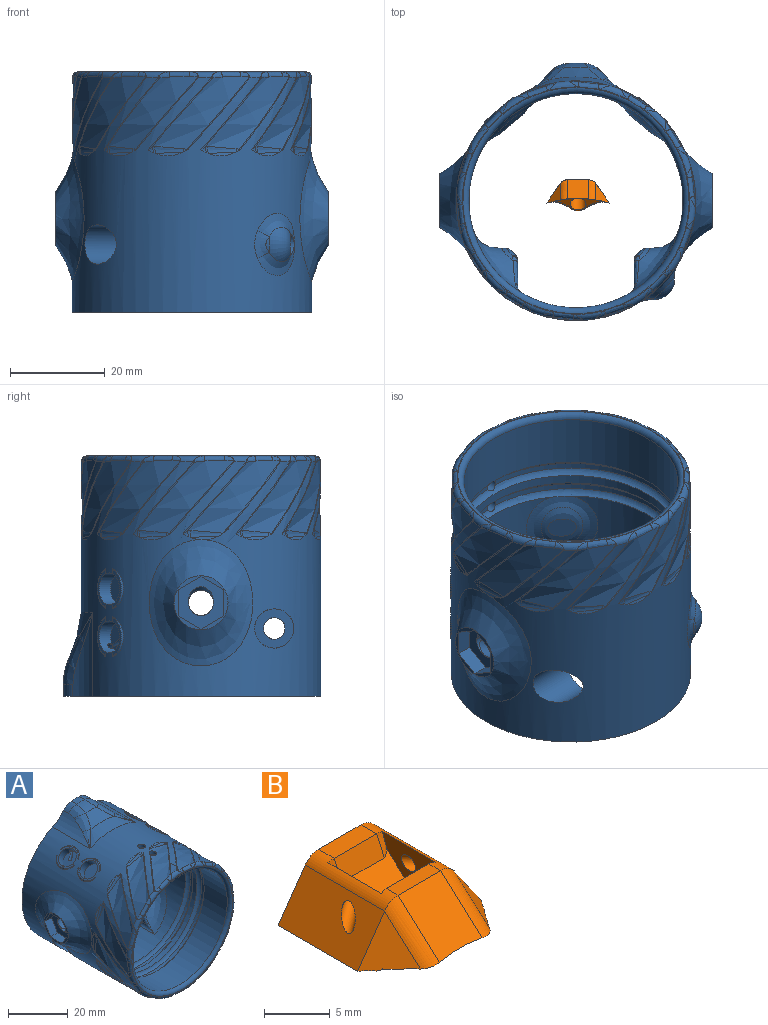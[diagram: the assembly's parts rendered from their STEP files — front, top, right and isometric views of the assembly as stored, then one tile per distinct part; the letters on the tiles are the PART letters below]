
ASSEMBLY  parts=2 mates=1
PART A: 355 faces, bbox 63.7x57.1x64.7 mm
  f0: torus R=24.04mm, axis (0,1,0), area 8.6mm2, adj f1,f340,f341,f342
  f1: bspline ~2.94x2.07mm, area 2.1mm2, adj f0,f2,f338,f339
  f2: bspline ~17.02x11.91mm, area 4.5mm2, adj f1,f3,f338,f342
  f3: bspline ~0.75x0.46mm, area 0mm2, adj f2,f4,f342
  f4: bspline ~0.8x0.72mm, area 0.3mm2, adj f3,f5,f338,f342
  f5: bspline ~7.78x2.13mm, area 6.8mm2, adj f4,f6,f337,f338
  f6: bspline ~1.52x0.62mm, area 0.7mm2, adj f5,f7,f338,f342
  f7: bspline ~1.74x1.53mm, area 0.7mm2, adj f6,f8,f342
  f8: bspline ~17.1x14.23mm, area 4.4mm2, adj f7,f9,f338,f342
  f9: bspline ~2.71x2.04mm, area 2.8mm2, adj f8,f10,f338,f339
  f10: torus R=24.04mm, axis (0,1,0), area 8.6mm2, adj f9,f11,f340,f342
  f11: bspline ~3.16x1.68mm, area 2.1mm2, adj f10,f12,f335,f336
  f12: bspline ~15.19x13mm, area 3.8mm2, adj f11,f13,f335,f342
  f13: cylinder r=1.27mm len=2.54mm, axis (0,0,-1), area 11.9mm2, adj f12,f14,f331,f334,f335,f342
  f14: torus R=22.14mm, axis (0,1,0), area 244.3mm2, adj f13,f15,f334
  f15: cylinder r=22.64mm len=45.29mm, axis (0,1,0), area 274.1mm2, adj f14,f16
  f16: torus R=22.14mm, axis (0,1,0), area 244.3mm2, adj f15,f17,f330
  f17: cylinder r=23.81mm len=47.63mm, axis (0,1,0), area 174.6mm2, adj f16,f18,f330
  f18: torus R=22.14mm, axis (0,1,0), area 243.9mm2, adj f17,f19,f25,f327,f330
  f19: bspline ~14.78x11.6mm, area 99.1mm2, adj f18,f20,f23,f25
  f20: bspline ~14.78x11.6mm, area 99.2mm2, adj f19,f21,f25
  f21: bspline ~9.62x6.81mm, area 48.2mm2, adj f20,f22
  f22: plane 4.62x4.43mm, normal (-0.64,0,-0.77), area 21.5mm2, adj f21
  f23: bspline ~9.62x6.81mm, area 48.2mm2, adj f19,f24
  f24: plane 4.62x4.43mm, normal (-0.64,0,-0.77), area 21.5mm2, adj f23
  f25: cylinder r=22.64mm len=45.29mm, axis (0,1,0), area 2511.8mm2, adj f18,f19,f20,f26,f52,f53,f54,f55
  f26: cylinder r=4.15mm len=8.31mm, axis (-1,0,0), area 147.8mm2, adj f25,f27,f40,f41,f42,f43,f44,f52
  f27: cylinder r=1.27mm len=1.9mm, axis (0,-1,0), area 0.9mm2, adj f26,f28,f40,f43
  f28: bspline ~1.21x1.2mm, area 0.4mm2, adj f27,f29,f39
  f29: bspline ~7.99x2.24mm, area 9.1mm2, adj f28,f30,f37,f38,f39,f43
  f30: cylinder r=5.42mm len=9.09mm, axis (-1,0,0), area 10.2mm2, adj f29,f31,f34,f53
  f31: torus R=4.41mm, axis (1,0,0), area 1.3mm2, adj f30,f32,f39,f40
  f32: bspline ~6.55x4.88mm, area 8.1mm2, adj f31,f33,f40,f53
  f33: bspline ~5.6x2.57mm, area 2.4mm2, adj f32,f52,f53
  f34: torus R=4.41mm, axis (1,0,0), area 1.3mm2, adj f30,f35,f37,f41
  f35: bspline ~6.55x4.88mm, area 8.1mm2, adj f34,f36,f41,f53
  f36: bspline ~4.89x2.08mm, area 2.4mm2, adj f35,f53,f54
  f37: bspline ~1.33x1.3mm, area 0.3mm2, adj f29,f34,f38,f41
  f38: bspline ~1.21x1.2mm, area 0.4mm2, adj f29,f37,f42
  f39: bspline ~1.05x0.91mm, area 0.3mm2, adj f28,f29,f31,f40
  f40: plane 5.75x4.22mm, normal (-1,0,0), area 6.7mm2, adj f26,f27,f31,f32,f39,f52
  f41: plane 5.74x4.21mm, normal (-1,0,0), area 6.7mm2, adj f26,f34,f35,f37,f42,f54
  f42: cylinder r=1.27mm len=1.9mm, axis (0,-1,0), area 0.9mm2, adj f26,f38,f41,f43
  f43: plane 6x1.48mm, normal (-0.71,0,0.71), area 5.5mm2, adj f26,f27,f29,f42
  f44: plane 8.31x8.31mm, normal (-1,0,0), area 37.8mm2, adj f26,f45
  f45: cylinder r=2.29mm len=4.57mm, axis (-1,0,0), area 44.4mm2, adj f44,f46,f49,f50,f51
  f46: torus R=0.85mm, axis (1,0,0), area 38mm2, adj f45,f47,f49,f51
  f47: cylinder r=5.42mm len=3.31mm, axis (-1,0,0), area 0mm2, adj f46,f48
  f48: bspline ~7.72x3.76mm, area 13.3mm2, adj f47,f49,f51,f342
  f49: bspline ~8.2x8.04mm, area 33.9mm2, adj f45,f46,f48,f50,f342
  f50: cylinder r=4.57mm len=1.7mm, axis (0,1,0), area 0.2mm2, adj f45,f49,f51,f342
  f51: bspline ~8.09x7.87mm, area 33.9mm2, adj f45,f46,f48,f50,f342
  f52: cylinder r=1.52mm len=10.75mm, axis (0,1,0), area 11.5mm2, adj f25,f26,f33,f40
  f53: bspline ~24.01x16.87mm, area 259.2mm2, adj f25,f30,f32,f33,f35,f36,f54
  f54: cylinder r=1.52mm len=10.75mm, axis (0,1,0), area 10.8mm2, adj f25,f26,f36,f41,f53
  f55: cylinder r=1.52mm len=10.75mm, axis (0,1,0), area 10.8mm2, adj f25,f56,f72,f73,f75
  f56: bspline ~4.89x2.08mm, area 2.4mm2, adj f55,f57,f75
  f57: bspline ~6.55x4.88mm, area 8.1mm2, adj f56,f58,f72,f75
  f58: torus R=4.41mm, axis (1,0,0), area 1.3mm2, adj f57,f59,f71,f72
  f59: bspline ~1.28x1.27mm, area 0.3mm2, adj f58,f60,f70,f72
  f60: bspline ~1.21x1.2mm, area 0.4mm2, adj f59,f61,f70
  f61: cylinder r=1.27mm len=1.9mm, axis (0,-1,0), area 0.9mm2, adj f60,f62,f72,f73
  f62: plane 6x1.48mm, normal (0.71,0,0.71), area 5.5mm2, adj f61,f63,f70,f73
  f63: cylinder r=1.27mm len=1.9mm, axis (0,-1,0), area 0.9mm2, adj f62,f64,f69,f73
  f64: plane 5.74x4.21mm, normal (1,0,0), area 6.7mm2, adj f63,f65,f67,f68,f73,f74
  f65: bspline ~6.55x4.88mm, area 8.1mm2, adj f64,f66,f67,f75
  f66: bspline ~5.6x2.57mm, area 2.4mm2, adj f65,f74,f75
  f67: torus R=4.41mm, axis (1,0,0), area 1.3mm2, adj f64,f65,f68,f71
  f68: bspline ~1.33x1.3mm, area 0.3mm2, adj f64,f67,f69,f70
  f69: bspline ~1.21x1.2mm, area 0.4mm2, adj f63,f68,f70
  f70: bspline ~7.99x2.24mm, area 9.1mm2, adj f59,f60,f62,f68,f69,f71
  f71: cylinder r=5.42mm len=9.09mm, axis (-1,0,0), area 10.2mm2, adj f58,f67,f70,f75
  f72: plane 5.75x4.22mm, normal (1,0,0), area 6.7mm2, adj f55,f57,f58,f59,f61,f73
  f73: cylinder r=4.15mm len=11.06mm, axis (-1,0,0), area 190.1mm2, adj f25,f55,f61,f62,f63,f64,f72,f74
  f74: cylinder r=1.52mm len=10.75mm, axis (0,1,0), area 11.5mm2, adj f25,f64,f66,f73
  f75: bspline ~24.01x16.87mm, area 259.2mm2, adj f25,f55,f56,f57,f65,f66,f71
  f76: cylinder r=5.71mm len=11.43mm, axis (1,0,0), area 14mm2, adj f25,f77
  f77: plane 17.49x17.49mm, normal (1,0,0), area 72.9mm2, adj f76,f78,f266
  f78: cylinder r=2.67mm len=5.33mm, axis (1,0,0), area 21.1mm2, adj f77,f79,f80,f266
  f79: cylinder r=2.63mm len=5.26mm, axis (-0.87,-0.48,0), area 0mm2, adj f78,f80
  f80: plane 13.99x12.5mm, normal (-1,0,0), area 55.1mm2, adj f78,f79,f81,f261,f262,f263,f264,f265
  f81: plane 4.85x3.32mm, normal (0,0.87,-0.5), area 18.4mm2, adj f80,f82,f260,f261,f265
  f82: plane 11.45x11.45mm, normal (-1,0,0), area 21.9mm2, adj f81,f83,f84,f260,f261,f262,f263,f264
  f83: cylinder r=2.63mm len=0.27mm, axis (-0.87,-0.48,0), area 0mm2, adj f82,f261
  f84: bspline ~26.69x21.89mm, area 456.4mm2, adj f82,f85,f342
  f85: bspline ~10.29x1.28mm, area 2.3mm2, adj f84,f86,f342
  f86: bspline ~9.05x1.63mm, area 7.1mm2, adj f85,f87,f258,f259,f342
  f87: bspline ~5.04x4.49mm, area 0.1mm2, adj f86,f88,f342
  f88: bspline ~16.54x13.1mm, area 4.2mm2, adj f87,f89,f258,f342
  f89: bspline ~3.13x1.68mm, area 2.1mm2, adj f88,f90,f229,f258
  f90: torus R=24.04mm, axis (0,1,0), area 8.6mm2, adj f89,f91,f340,f342
  f91: bspline ~2.91x1.57mm, area 2.8mm2, adj f90,f92,f227,f228
  f92: bspline ~7.63x5.22mm, area 6.7mm2, adj f91,f93,f227,f340
  f93: bspline ~2.61x2.46mm, area 2.1mm2, adj f92,f94,f220,f227
  f94: torus R=24.04mm, axis (0,1,0), area 8.6mm2, adj f93,f95,f340,f342
  f95: bspline ~2.87x1.53mm, area 2.8mm2, adj f94,f96,f218,f219
  f96: bspline ~8.34x1.89mm, area 6.7mm2, adj f95,f97,f218,f340
  f97: bspline ~2.88x1.68mm, area 2.1mm2, adj f96,f98,f211,f218
  f98: torus R=24.04mm, axis (0,1,0), area 8.6mm2, adj f97,f99,f340,f342
  f99: bspline ~2.65x1.92mm, area 2.8mm2, adj f98,f100,f209,f210
  f100: bspline ~8.12x3.87mm, area 6.7mm2, adj f99,f101,f209,f340
  f101: bspline ~3.16x1.68mm, area 2.1mm2, adj f100,f102,f202,f209
  f102: torus R=24.04mm, axis (0,1,0), area 8.6mm2, adj f101,f103,f340,f342
  f103: bspline ~2.71x2.04mm, area 2.8mm2, adj f102,f104,f200,f201
  f104: bspline ~6.69x6.53mm, area 6.7mm2, adj f103,f105,f200,f340
  f105: bspline ~2.94x2.07mm, area 2.1mm2, adj f104,f106,f193,f200
  f106: torus R=24.04mm, axis (0,1,0), area 8.6mm2, adj f105,f107,f340,f342
  f107: bspline ~2.96x1.53mm, area 2.8mm2, adj f106,f108,f191,f192
  f108: bspline ~6.73x3.14mm, area 6.7mm2, adj f107,f109,f191,f340
  f109: bspline ~2.74x2.14mm, area 2.1mm2, adj f108,f110,f184,f191
  f110: torus R=24.04mm, axis (0,1,0), area 8.6mm2, adj f109,f111,f340,f342
  f111: bspline ~2.76x1.53mm, area 2.8mm2, adj f110,f112,f182,f183
  f112: bspline ~8.32x2.12mm, area 6.7mm2, adj f111,f113,f182,f340
  f113: bspline ~3.03x1.68mm, area 2.1mm2, adj f112,f114,f175,f182
  f114: torus R=24.04mm, axis (0,1,0), area 8.6mm2, adj f113,f115,f340,f342
  f115: bspline ~2.4x2.38mm, area 2.8mm2, adj f114,f116,f173,f174
  f116: bspline ~7.51x5.42mm, area 6.7mm2, adj f115,f117,f173,f340
  f117: bspline ~3.13x1.68mm, area 2.1mm2, adj f116,f118,f152,f173
  f118: torus R=24.04mm, axis (0,1,0), area 8.6mm2, adj f117,f119,f340,f342
  f119: bspline ~2.91x1.57mm, area 2.8mm2, adj f118,f120,f150,f151
  f120: bspline ~7.63x5.22mm, area 6.7mm2, adj f119,f121,f150,f340
  f121: bspline ~2.61x2.46mm, area 2.1mm2, adj f120,f122,f143,f150
  f122: torus R=24.04mm, axis (0,1,0), area 8.6mm2, adj f121,f123,f340,f342
  f123: bspline ~2.87x1.53mm, area 2.8mm2, adj f122,f124,f141,f142
  f124: bspline ~8.34x1.89mm, area 6.7mm2, adj f123,f125,f141,f340
  f125: bspline ~2.88x1.68mm, area 2.1mm2, adj f124,f126,f134,f141
  f126: torus R=24.04mm, axis (0,1,0), area 8.6mm2, adj f125,f127,f133,f340
  f127: bspline ~2.65x1.92mm, area 2.8mm2, adj f126,f128,f335,f336
  f128: bspline ~17.1x15mm, area 4.4mm2, adj f127,f129,f133,f335,f342
  f129: bspline ~1.74x1.45mm, area 0.7mm2, adj f128,f130,f342
  f130: bspline ~1.52x0.58mm, area 0.7mm2, adj f129,f131,f335,f342
  f131: bspline ~8.28x1.82mm, area 7.1mm2, adj f130,f132,f335,f342
  f132: bspline ~10.13x2.46mm, area 0mm2, adj f131,f342
  f133: cylinder r=25.31mm len=4.47mm, axis (0,1,0), area 8mm2, adj f126,f128,f134,f342
  f134: bspline ~17.55x15.05mm, area 4.5mm2, adj f125,f133,f135,f141,f342
  f135: bspline ~0.71x0.46mm, area 0mm2, adj f134,f136,f342
  f136: bspline ~0.72x0.67mm, area 0.3mm2, adj f135,f137,f141,f342
  f137: bspline ~6.43x4.94mm, area 6.8mm2, adj f136,f138,f140,f141
  f138: bspline ~1.52x0.47mm, area 0.7mm2, adj f137,f139,f141,f342
  f139: bspline ~1.74x1.1mm, area 0.7mm2, adj f138,f142,f342
  f140: bspline ~8.36x6.55mm, area 0mm2, adj f137,f342
  f141: bspline ~24.34x17.78mm, area 120.3mm2, adj f123,f124,f125,f134,f136,f137,f138,f142
  f142: bspline ~17.1x12.79mm, area 4.4mm2, adj f123,f139,f141,f342
  f143: bspline ~17.55x12.01mm, area 4.5mm2, adj f121,f144,f150,f342
  f144: bspline ~0.66x0.48mm, area 0mm2, adj f143,f145,f342
  f145: bspline ~0.74x0.72mm, area 0.3mm2, adj f144,f146,f150,f342
  f146: bspline ~7.17x3.77mm, area 6.8mm2, adj f145,f147,f149,f150
  f147: bspline ~1.52x0.59mm, area 0.7mm2, adj f146,f148,f150,f342
  f148: bspline ~1.74x1.46mm, area 0.7mm2, adj f147,f151,f342
  f149: bspline ~9.34x4.93mm, area 0mm2, adj f146,f342
  f150: bspline ~19.46x17.78mm, area 120.3mm2, adj f119,f120,f121,f143,f145,f146,f147,f151
  f151: bspline ~17.1x12.76mm, area 4.4mm2, adj f119,f148,f150,f342
  f152: bspline ~16.54x13.1mm, area 4.2mm2, adj f117,f153,f173,f342
  f153: bspline ~5.07x4.52mm, area 0.1mm2, adj f152,f154,f342
  f154: bspline ~9.06x1.63mm, area 7.1mm2, adj f153,f155,f157,f173,f342
  f155: bspline ~1.52x0.62mm, area 0.7mm2, adj f154,f156,f173,f342
  f156: bspline ~1.74x1.53mm, area 0.7mm2, adj f155,f174,f342
  f157: bspline ~10.29x1.28mm, area 2.5mm2, adj f154,f158,f342
  f158: bspline ~26.69x21.9mm, area 456.4mm2, adj f157,f159,f342
  f159: plane 11.92x11.92mm, normal (1,0,0), area 22mm2, adj f158,f160,f166,f167,f168,f169,f170,f171
  f160: plane 5.57x3.3mm, normal (0,0,1), area 18.4mm2, adj f159,f161,f166,f171
  f161: plane 13.99x12.5mm, normal (1,0,0), area 55.1mm2, adj f160,f162,f165,f166,f167,f168,f170,f171
  f162: cylinder r=2.67mm len=5.33mm, axis (1,0,0), area 21.1mm2, adj f161,f163,f164,f165
  f163: plane 17.49x17.49mm, normal (-1,0,0), area 72.9mm2, adj f162,f164,f267
  f164: cylinder r=2.63mm len=5.26mm, axis (0.87,-0.48,0), area 0mm2, adj f162,f163
  f165: cylinder r=2.63mm len=5.26mm, axis (0.87,-0.48,0), area 0mm2, adj f161,f162
  f166: plane 4.83x3.3mm, normal (0,-0.87,0.5), area 18.4mm2, adj f159,f160,f161,f167
  f167: plane 4.83x3.3mm, normal (0,-0.87,-0.5), area 18.4mm2, adj f159,f161,f166,f168
  f168: plane 5.57x3.3mm, normal (0,0,-1), area 18.4mm2, adj f159,f161,f167,f170
  f169: cylinder r=2.63mm len=0.27mm, axis (0.87,-0.48,0), area 0mm2, adj f159,f170
  f170: plane 4.85x3.32mm, normal (0,0.87,-0.5), area 18.4mm2, adj f159,f161,f168,f169,f171
  f171: plane 4.85x3.32mm, normal (0,0.87,0.5), area 18.4mm2, adj f159,f160,f161,f170,f172
  f172: cylinder r=2.63mm len=0.27mm, axis (0.87,-0.48,0), area 0mm2, adj f159,f171
  f173: bspline ~25.19x17.78mm, area 120.2mm2, adj f115,f116,f117,f152,f154,f155,f174
  f174: bspline ~17.1x14.99mm, area 4.4mm2, adj f115,f156,f173,f342
  f175: bspline ~17.55x15.47mm, area 4.5mm2, adj f113,f176,f182,f342
  f176: bspline ~0.78x0.46mm, area 0mm2, adj f175,f177,f342
  f177: bspline ~0.74x0.72mm, area 0.3mm2, adj f176,f178,f182,f342
  f178: bspline ~7.32x3.42mm, area 6.8mm2, adj f177,f179,f181,f182
  f179: bspline ~1.52x0.53mm, area 0.7mm2, adj f178,f180,f182,f342
  f180: bspline ~1.74x1.29mm, area 0.7mm2, adj f179,f183,f342
  f181: bspline ~9.48x4.62mm, area 0mm2, adj f178,f342
  f182: bspline ~25.93x17.78mm, area 120.3mm2, adj f111,f112,f113,f175,f177,f178,f179,f183
  f183: bspline ~17.1x14.25mm, area 4.4mm2, adj f111,f180,f182,f342
  f184: bspline ~17.55x13.88mm, area 4.5mm2, adj f109,f185,f191,f342
  f185: bspline ~0.61x0.54mm, area 0mm2, adj f184,f186,f342
  f186: bspline ~0.72x0.64mm, area 0.3mm2, adj f185,f187,f191,f342
  f187: bspline ~6.21x5.21mm, area 6.8mm2, adj f186,f188,f190,f191
  f188: bspline ~1.52x0.54mm, area 0.7mm2, adj f187,f189,f191,f342
  f189: bspline ~1.74x1.31mm, area 0.7mm2, adj f188,f192,f342
  f190: bspline ~8.15x6.81mm, area 0mm2, adj f187,f342
  f191: bspline ~21.54x17.78mm, area 120.3mm2, adj f107,f108,f109,f184,f186,f187,f188,f192
  f192: bspline ~17.1x10.69mm, area 4.4mm2, adj f107,f189,f191,f342
  f193: bspline ~17.02x11.91mm, area 4.5mm2, adj f105,f194,f200,f342
  f194: bspline ~0.75x0.46mm, area 0mm2, adj f193,f195,f342
  f195: bspline ~0.8x0.72mm, area 0.3mm2, adj f194,f196,f200,f342
  f196: bspline ~7.78x2.13mm, area 6.8mm2, adj f195,f197,f199,f200
  f197: bspline ~1.52x0.62mm, area 0.7mm2, adj f196,f198,f200,f342
  f198: bspline ~1.74x1.53mm, area 0.7mm2, adj f197,f201,f342
  f199: bspline ~10.07x2.79mm, area 0mm2, adj f196,f342
  f200: bspline ~22.9x17.78mm, area 120.3mm2, adj f103,f104,f105,f193,f195,f196,f197,f201
  f201: bspline ~17.1x14.23mm, area 4.4mm2, adj f103,f198,f200,f342
  f202: bspline ~17.55x15.11mm, area 4.5mm2, adj f101,f203,f209,f342
  f203: bspline ~0.81x0.46mm, area 0mm2, adj f202,f204,f342
  f204: bspline ~0.79x0.72mm, area 0.3mm2, adj f203,f205,f209,f342
  f205: bspline ~7.86x1.74mm, area 6.8mm2, adj f204,f206,f208,f209
  f206: bspline ~1.52x0.58mm, area 0.7mm2, adj f205,f207,f209,f342
  f207: bspline ~1.74x1.45mm, area 0.7mm2, adj f206,f210,f342
  f208: bspline ~10.13x2.46mm, area 0mm2, adj f205,f342
  f209: bspline ~26.22x17.78mm, area 120.3mm2, adj f99,f100,f101,f202,f204,f205,f206,f210
  f210: bspline ~17.1x15mm, area 4.4mm2, adj f99,f207,f209,f342
  f211: bspline ~17.55x15.05mm, area 4.5mm2, adj f97,f212,f218,f342
  f212: bspline ~0.71x0.46mm, area 0mm2, adj f211,f213,f342
  f213: bspline ~0.72x0.67mm, area 0.3mm2, adj f212,f214,f218,f342
  f214: bspline ~6.43x4.94mm, area 6.8mm2, adj f213,f215,f217,f218
  f215: bspline ~1.52x0.47mm, area 0.7mm2, adj f214,f216,f218,f342
  f216: bspline ~1.74x1.1mm, area 0.7mm2, adj f215,f219,f342
  f217: bspline ~8.36x6.55mm, area 0mm2, adj f214,f342
  f218: bspline ~24.34x17.78mm, area 120.3mm2, adj f95,f96,f97,f211,f213,f214,f215,f219
  f219: bspline ~17.1x12.79mm, area 4.4mm2, adj f95,f216,f218,f342
  f220: bspline ~17.55x12.01mm, area 4.5mm2, adj f93,f221,f227,f342
  f221: bspline ~0.66x0.48mm, area 0mm2, adj f220,f222,f342
  f222: bspline ~0.74x0.72mm, area 0.3mm2, adj f221,f223,f227,f342
  f223: bspline ~7.17x3.77mm, area 6.8mm2, adj f222,f224,f226,f227
  f224: bspline ~1.52x0.59mm, area 0.7mm2, adj f223,f225,f227,f342
  f225: bspline ~1.74x1.46mm, area 0.7mm2, adj f224,f228,f342
  f226: bspline ~9.34x4.93mm, area 0mm2, adj f223,f342
  f227: bspline ~19.46x17.78mm, area 120.3mm2, adj f91,f92,f93,f220,f222,f223,f224,f228
  f228: bspline ~17.1x12.76mm, area 4.4mm2, adj f91,f225,f227,f342
  f229: bspline ~7.51x5.42mm, area 6.7mm2, adj f89,f230,f258,f340
  f230: bspline ~2.4x2.38mm, area 2.8mm2, adj f229,f231,f256,f258
  f231: torus R=24.04mm, axis (0,1,0), area 8.6mm2, adj f230,f232,f340,f342
  f232: bspline ~3.03x1.68mm, area 2.1mm2, adj f231,f233,f254,f255
  f233: bspline ~17.55x15.47mm, area 4.5mm2, adj f232,f234,f254,f342
  f234: bspline ~0.78x0.46mm, area 0mm2, adj f233,f235,f342
  f235: bspline ~0.74x0.72mm, area 0.3mm2, adj f234,f236,f254,f342
  f236: bspline ~7.32x3.42mm, area 6.8mm2, adj f235,f237,f253,f254
  f237: bspline ~1.52x0.53mm, area 0.7mm2, adj f236,f238,f254,f342
  f238: bspline ~1.74x1.29mm, area 0.7mm2, adj f237,f239,f342
  f239: bspline ~17.1x14.25mm, area 4.4mm2, adj f238,f240,f254,f342
  f240: bspline ~2.76x1.53mm, area 2.8mm2, adj f239,f241,f254,f255
  f241: torus R=24.04mm, axis (0,1,0), area 8.6mm2, adj f240,f242,f340,f342
  f242: bspline ~2.74x2.14mm, area 2.1mm2, adj f241,f243,f251,f252
  f243: bspline ~17.55x13.88mm, area 4.5mm2, adj f242,f244,f251,f342
  f244: bspline ~0.61x0.54mm, area 0mm2, adj f243,f245,f342
  f245: bspline ~0.72x0.64mm, area 0.3mm2, adj f244,f246,f251,f342
  f246: bspline ~6.21x5.21mm, area 6.8mm2, adj f245,f247,f250,f251
  f247: bspline ~1.52x0.54mm, area 0.7mm2, adj f246,f248,f251,f342
  f248: bspline ~1.74x1.31mm, area 0.7mm2, adj f247,f249,f342
  f249: bspline ~17.1x10.69mm, area 4.4mm2, adj f248,f251,f341,f342
  f250: bspline ~8.15x6.81mm, area 0mm2, adj f246,f342
  f251: bspline ~21.54x17.78mm, area 120.3mm2, adj f242,f243,f245,f246,f247,f249,f252,f341
  f252: bspline ~6.73x3.14mm, area 6.7mm2, adj f242,f251,f340,f341
  f253: bspline ~9.48x4.62mm, area 0mm2, adj f236,f342
  f254: bspline ~25.93x17.78mm, area 120.3mm2, adj f232,f233,f235,f236,f237,f239,f240,f255
  f255: bspline ~8.32x2.12mm, area 6.7mm2, adj f232,f240,f254,f340
  f256: bspline ~17.1x14.99mm, area 4.4mm2, adj f230,f257,f258,f342
  f257: bspline ~1.74x1.53mm, area 0.7mm2, adj f256,f259,f342
  f258: bspline ~25.19x17.78mm, area 120.2mm2, adj f86,f88,f89,f229,f230,f256,f259
  f259: bspline ~1.52x0.62mm, area 0.7mm2, adj f86,f257,f258,f342
  f260: cylinder r=2.63mm len=0.27mm, axis (-0.87,-0.48,0), area 0mm2, adj f81,f82
  f261: plane 4.85x3.32mm, normal (0,0.87,0.5), area 18.4mm2, adj f80,f81,f82,f83,f262
  f262: plane 5.57x3.3mm, normal (0,0,1), area 18.4mm2, adj f80,f82,f261,f263
  f263: plane 4.83x3.3mm, normal (0,-0.87,0.5), area 18.4mm2, adj f80,f82,f262,f264
  f264: plane 4.83x3.3mm, normal (0,-0.87,-0.5), area 18.4mm2, adj f80,f82,f263,f265
  f265: plane 5.57x3.3mm, normal (0,0,-1), area 18.4mm2, adj f80,f81,f82,f264
  f266: cylinder r=2.63mm len=5.26mm, axis (-0.87,-0.48,0), area 0mm2, adj f77,f78
  f267: cylinder r=5.71mm len=11.43mm, axis (1,0,0), area 14mm2, adj f25,f163
  f268: plane 5.1x5.03mm, normal (0.73,0.46,-0.51), area 16.4mm2, adj f25,f269,f285,f286,f287
  f269: plane 8.23x0.69mm, normal (0,-0.74,-0.67), area 0.7mm2, adj f268,f270,f273,f274,f281,f282,f284,f285
  f270: plane 4.06x3.42mm, normal (0.16,-0.99,0.04), area 1.4mm2, adj f269,f271,f272,f273,f293
  f271: plane 0.89x0.87mm, normal (0.23,-0.65,0.72), area 0.3mm2, adj f270,f272,f293,f294
  f272: plane 4.19x2.94mm, normal (0.73,-0.46,0.51), area 1mm2, adj f270,f271,f273,f274,f294
  f273: extruded ~0.4x0.32mm, area 0mm2, adj f269,f270,f272,f274
  f274: cylinder r=2.03mm len=8.49mm, axis (0,1,0), area 14.4mm2, adj f269,f272,f273,f275,f278,f279,f280,f281
  f275: plane 5.9x0.63mm, normal (0,0.67,-0.74), area 3.7mm2, adj f274,f276,f277,f278,f281,f282
  f276: cylinder r=1.27mm len=5.84mm, axis (-1,0,0), area 11.7mm2, adj f275,f277,f278,f279
  f277: plane 2.76x0.85mm, normal (1,0,0), area 1.5mm2, adj f275,f276,f279,f282
  f278: plane 2.76x0.85mm, normal (-1,0,0), area 1.5mm2, adj f274,f275,f276,f279
  f279: plane 5.89x0.48mm, normal (0,-0.74,-0.67), area 2.6mm2, adj f274,f276,f277,f278,f280,f282
  f280: plane 4.57x4.45mm, normal (0,0,-1), area 20.3mm2, adj f274,f279,f282,f303
  f281: plane 4.57x1.49mm, normal (0,0,-1), area 6.8mm2, adj f269,f274,f275,f282
  f282: cylinder r=2.03mm len=8.49mm, axis (0,1,0), area 14.4mm2, adj f269,f275,f277,f279,f280,f281,f283,f284
  f283: plane 4.19x2.94mm, normal (-0.73,-0.46,0.51), area 1mm2, adj f282,f284,f285,f286,f318
  f284: extruded ~0.4x0.32mm, area 0mm2, adj f269,f282,f283,f285
  f285: plane 4.06x3.42mm, normal (-0.16,-0.99,0.04), area 1.4mm2, adj f268,f269,f283,f284,f286
  f286: plane 0.89x0.87mm, normal (-0.23,-0.65,0.72), area 0.3mm2, adj f268,f283,f285,f318
  f287: extruded ~5.22x4.81mm, area 11.5mm2, adj f25,f268,f269,f291
  f288: bspline ~14.78x11.6mm, area 99.2mm2, adj f25,f289,f327
  f289: bspline ~9.62x6.81mm, area 48.2mm2, adj f288,f290
  f290: plane 4.62x4.43mm, normal (0.64,0,-0.77), area 21.5mm2, adj f289
  f291: plane 4.93x4.71mm, normal (0,0.67,-0.74), area 29mm2, adj f25,f269,f287,f292
  f292: extruded ~5.22x4.81mm, area 11.5mm2, adj f25,f269,f291,f293
  f293: plane 5.1x5.03mm, normal (-0.73,0.46,-0.51), area 16.4mm2, adj f25,f269,f270,f271,f292
  f294: plane 8.56x4.44mm, normal (-0.82,0,-0.57), area 41.3mm2, adj f25,f271,f272,f274,f295,f303
  f295: torus R=23.74mm, axis (-0.55,-0.83,-0.04), area 44.2mm2, adj f294,f296,f301,f302
  f296: cylinder r=3.37mm len=7.2mm, axis (0.64,0,0.77), area 65.9mm2, adj f295,f297,f299,f301,f342
  f297: plane 9.44x3.14mm, normal (0.64,0,0.77), area 6.4mm2, adj f296,f298,f342
  f298: bspline ~8.68x3.45mm, area 0.1mm2, adj f297,f342
  f299: plane 9.44x3.14mm, normal (0.64,0,0.77), area 6.4mm2, adj f296,f300,f342
  f300: bspline ~8.68x3.09mm, area 0.1mm2, adj f299,f342
  f301: plane 6.79x5.22mm, normal (0.64,0,0.77), area 32.3mm2, adj f295,f296,f302
  f302: plane 1.2x0.68mm, normal (-0.55,0.33,0.77), area 0.6mm2, adj f295,f301
  f303: plane 54.43x50.62mm, normal (0,1,0), area 405.4mm2, adj f25,f274,f280,f282,f294,f304,f314,f315
  f304: cylinder r=13.97mm len=17.77mm, axis (0,1,0), area 75.7mm2, adj f303,f305,f312,f313,f314,f342
  f305: bspline ~9.36x4.49mm, area 18.1mm2, adj f304,f306,f312,f314
  f306: torus R=15.15mm, axis (0,-1,0), area 22.5mm2, adj f305,f307,f311,f315
  f307: cone r=29.12mm half-angle=20.6deg, axis (0,1,0), area 46.9mm2, adj f306,f308,f310,f312
  f308: torus R=39.28mm, axis (0,1,0), area 83.4mm2, adj f307,f309,f313,f342
  f309: bspline ~6.69x5.34mm, area 7.6mm2, adj f308,f310,f317
  f310: bspline ~10.91x6.7mm, area 23.3mm2, adj f307,f309,f311,f317
  f311: bspline ~7.83x4.14mm, area 18.1mm2, adj f306,f310,f316,f317
  f312: bspline ~9.02x6.04mm, area 23.3mm2, adj f304,f305,f307,f313
  f313: bspline ~6.69x5.34mm, area 7.6mm2, adj f304,f308,f312
  f314: cylinder r=5.08mm len=3.7mm, axis (0,-1,0), area 11mm2, adj f303,f304,f305,f315
  f315: cylinder r=29.12mm len=3.9mm, axis (0,1,0), area 9.9mm2, adj f303,f306,f314,f316
  f316: cylinder r=5.08mm len=3.7mm, axis (0,1,0), area 11mm2, adj f303,f311,f315,f317
  f317: cylinder r=13.97mm len=17.77mm, axis (0,1,0), area 75.7mm2, adj f303,f309,f310,f311,f316,f342
  f318: plane 8.56x4.44mm, normal (0.82,0,-0.57), area 41.3mm2, adj f25,f282,f283,f286,f303,f319
  f319: torus R=23.74mm, axis (0.55,-0.83,-0.04), area 44.2mm2, adj f318,f320,f325,f326
  f320: cylinder r=3.37mm len=7.2mm, axis (-0.64,0,0.77), area 65.8mm2, adj f319,f321,f323,f325,f342
  f321: plane 9.44x3.14mm, normal (-0.64,0,0.77), area 6.4mm2, adj f320,f322,f342
  f322: bspline ~8.68x3.09mm, area 0.1mm2, adj f321,f342
  f323: plane 9.44x3.14mm, normal (-0.64,0,0.77), area 6.4mm2, adj f320,f324,f342
  f324: bspline ~8.68x3.45mm, area 0.1mm2, adj f323,f342
  f325: plane 6.79x5.22mm, normal (-0.64,0,0.77), area 32.3mm2, adj f319,f320,f326
  f326: plane 1.2x0.68mm, normal (0.55,0.33,0.77), area 0.6mm2, adj f319,f325
  f327: bspline ~14.78x11.6mm, area 99.1mm2, adj f18,f25,f288,f328
  f328: bspline ~9.62x6.81mm, area 48.2mm2, adj f327,f329
  f329: plane 4.62x4.43mm, normal (0.64,0,-0.77), area 21.5mm2, adj f328
  f330: cylinder r=1.27mm len=2.54mm, axis (0,0,-1), area 13.4mm2, adj f16,f17,f18,f342
  f331: torus R=22.14mm, axis (0,1,0), area 244.3mm2, adj f13,f332,f334
  f332: cylinder r=22.64mm len=45.29mm, axis (0,1,0), area 1564.5mm2, adj f331,f333
  f333: torus R=23.91mm, axis (0,1,0), area 289.6mm2, adj f332,f340
  f334: cylinder r=23.81mm len=47.63mm, axis (0,1,0), area 174.5mm2, adj f13,f14,f331
  f335: bspline ~26.22x17.78mm, area 115.9mm2, adj f11,f12,f13,f127,f128,f130,f131,f336
  f336: bspline ~8.12x3.87mm, area 6.7mm2, adj f11,f127,f335,f340
  f337: bspline ~10.07x2.79mm, area 0mm2, adj f5,f342
  f338: bspline ~22.9x17.78mm, area 120.3mm2, adj f1,f2,f4,f5,f6,f8,f9,f339
  f339: bspline ~6.69x6.53mm, area 6.7mm2, adj f1,f9,f338,f340
  f340: plane 48.08x48.08mm, normal (0,-1,0), area 15.6mm2, adj f0,f10,f90,f92,f94,f96,f98,f100
  f341: bspline ~2.96x1.53mm, area 2.8mm2, adj f0,f249,f251,f252
  f342: cylinder r=25.31mm len=50.62mm, axis (0,1,0), area 4152.5mm2, adj f0,f2,f3,f4,f6,f7,f8,f10
  f343: bspline ~8.68x3.09mm, area 0.1mm2, adj f342,f344
  f344: plane 9.44x3.14mm, normal (-0.64,0,0.77), area 6.4mm2, adj f342,f343,f345
  f345: cylinder r=3.37mm len=7.2mm, axis (-0.64,0,0.77), area 67.1mm2, adj f342,f344,f346,f347
  f346: plane 6.73x5.16mm, normal (-0.64,0,0.77), area 35.6mm2, adj f345
  f347: plane 9.44x3.14mm, normal (-0.64,0,0.77), area 6.4mm2, adj f342,f345,f348
  f348: bspline ~8.68x3.45mm, area 0.1mm2, adj f342,f347
  f349: bspline ~8.68x3.45mm, area 0.1mm2, adj f342,f350
  f350: plane 9.44x3.14mm, normal (0.64,0,0.77), area 6.4mm2, adj f342,f349,f351
  f351: cylinder r=3.37mm len=7.2mm, axis (0.64,0,0.77), area 67.1mm2, adj f342,f350,f352,f353
  f352: plane 6.73x5.16mm, normal (0.64,0,0.77), area 35.6mm2, adj f351
  f353: plane 9.44x3.14mm, normal (0.64,0,0.77), area 6.4mm2, adj f342,f351,f354
  f354: bspline ~8.68x3.09mm, area 0.1mm2, adj f342,f353
PART B: 32 faces, bbox 13.8x13.3x8 mm
  f0: plane 4.86x2.14mm, normal (0,-0.74,-0.67), area 4.2mm2, adj f1,f5,f29
  f1: cylinder r=22.64mm len=11.04mm, axis (0,1,0), area 21.6mm2, adj f0,f5,f16,f17,f18,f19,f20,f24
  f2: cylinder r=22.64mm len=13.32mm, axis (0,1,0), area 71.9mm2, adj f10,f11,f15,f16,f20,f26
  f3: plane 6.08x2.54mm, normal (0,-0.67,0.74), area 15.4mm2, adj f4,f6,f8,f21,f22,f23
  f4: plane 5.84x3.39mm, normal (0,0.74,0.67), area 17.9mm2, adj f3,f5,f6,f8,f9
  f5: cylinder r=1.68mm len=5.85mm, axis (0,-0.74,-0.67), area 51.1mm2, adj f0,f1,f4,f24,f28
  f6: plane 6.11x3.72mm, normal (-1,0,0), area 9.7mm2, adj f3,f4,f9,f14,f21,f30
  f7: plane 4.57x1.68mm, normal (0,0,1), area 7.7mm2, adj f10,f12,f14,f22
  f8: plane 6.11x3.72mm, normal (1,0,0), area 9.7mm2, adj f3,f4,f9,f12,f23,f31
  f9: plane 5.91x0.26mm, normal (0,0.67,-0.74), area 1.5mm2, adj f4,f6,f8,f12,f13,f14
  f10: plane 13.32x4.93mm, normal (0,1,0), area 39.5mm2, adj f2,f7,f11,f12,f14,f15
  f11: plane 8.56x4.17mm, normal (-0.82,0,0.57), area 41mm2, adj f2,f10,f12,f16,f31
  f12: cylinder r=1.78mm len=8.56mm, axis (0,1,0), area 10.9mm2, adj f7,f8,f9,f10,f11,f13,f17,f23
  f13: plane 4.57x1.28mm, normal (0,0,1), area 5.8mm2, adj f9,f12,f14,f18
  f14: cylinder r=1.78mm len=8.56mm, axis (0,1,0), area 10.9mm2, adj f6,f7,f9,f10,f13,f15,f19,f21
  f15: plane 8.56x4.17mm, normal (0.82,0,0.57), area 41mm2, adj f2,f10,f14,f20,f30
  f16: plane 4.22x3.9mm, normal (-0.73,-0.46,0.51), area 10.9mm2, adj f1,f2,f11,f17,f26,f27
  f17: extruded ~4.85x4.46mm, area 9mm2, adj f1,f12,f16,f18
  f18: plane 4.57x4.47mm, normal (0,-0.67,0.74), area 27mm2, adj f1,f13,f17,f19
  f19: extruded ~4.85x4.46mm, area 9mm2, adj f1,f14,f18,f20
  f20: plane 4.22x3.9mm, normal (0.73,-0.46,0.51), area 10.9mm2, adj f1,f2,f15,f19,f26,f29
  f21: bspline ~2.18x1.54mm, area 1.2mm2, adj f3,f6,f14,f22
  f22: plane 4.57x1.83mm, normal (0,-0.91,0.41), area 9.2mm2, adj f3,f7,f21,f23
  f23: bspline ~2.18x1.54mm, area 1.2mm2, adj f3,f8,f12,f22
  f24: plane 4.86x2.14mm, normal (0,-0.74,-0.67), area 4.2mm2, adj f1,f5,f27
  f25: cylinder r=2.18mm len=2.86mm, axis (0,0.74,0.67), area 4.6mm2, adj f26,f28
  f26: bspline ~13.51x7.89mm, area 47.8mm2, adj f2,f16,f20,f25,f27,f29
  f27: bspline ~5.61x2.35mm, area 3mm2, adj f1,f16,f24,f26,f28
  f28: torus R=1.68mm, axis (0,0.74,0.67), area 2.3mm2, adj f5,f25,f27,f29
  f29: bspline ~5.61x2.35mm, area 3mm2, adj f0,f1,f20,f26,f28
  f30: torus R=23.74mm, axis (-0.55,-0.83,-0.04), area 9.2mm2, adj f6,f15
  f31: torus R=23.74mm, axis (0.55,-0.83,-0.04), area 9.2mm2, adj f8,f11
PLACE A rot(axis=(-1,0,0),90deg) t=(-25.58,10.52,17.72)mm
PLACE B rot(axis=(-1,0,0),90deg) t=(-25.14,-11.59,17.72)mm
MATE planar B.f10 <-> A.f303  axis (0,0,-1) through (-25.14,12.61,-15.55)mm
